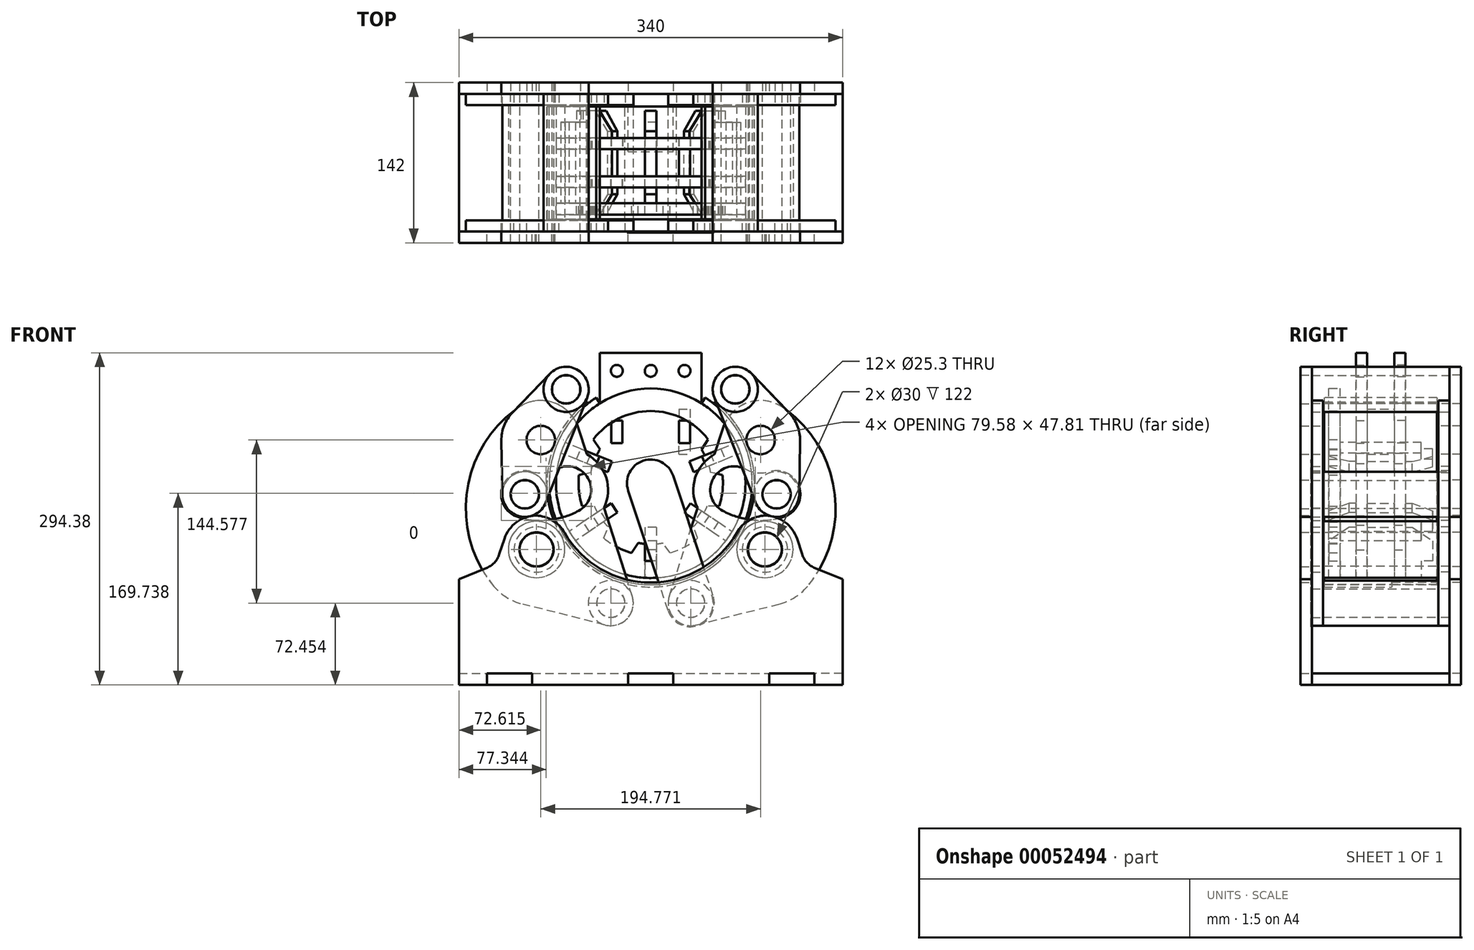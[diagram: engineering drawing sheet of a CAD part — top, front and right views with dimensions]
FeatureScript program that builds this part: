
annotation { "Feature Type Name" : "Feature", "Feature Type Description" : "" }
export const myFeature = defineFeature(function(context is Context, id is Id, definition is map)
    precondition{}
    {
        {
            var Q0;
            Q0=qCreatedBy(makeId("Front.planeOp"),FACE);
            var sketch = newSketch(context, id + "F0", { "sketchPlane" : qUnion([Q0])});
            skCircle(sketch, "E0", {"center": v(0, 0) * mm, "radius": 90 * mm, "construction": true});
            skLineSegment(sketch, "E1", {"start": v(0, -90) * mm, "end": v(0, 90) * mm, "construction": true});
            skLineSegment(sketch, "E2", {"start": v(0, 0) * mm, "end": v(-55.75, 70.66) * mm, "construction": true});
            skLineSegment(sketch, "E3", {"start": v(0, 0) * mm, "end": v(55.75, 70.66) * mm, "construction": true});
            skArc(sketch, "E4", {"start": v(-55.75, 70.66) * mm, "mid": v(0, -90) * mm, "end": v(55.75, 70.66) * mm});
            skArc(sketch, "E5", {"start": v(-56.98, 72.23) * mm, "mid": v(0, -92) * mm, "end": v(56.98, 72.23) * mm});
            skLineSegment(sketch, "E6", {"start": v(-56.98, 72.23) * mm, "end": v(-55.75, 70.66) * mm});
            skLineSegment(sketch, "E7", {"start": v(55.75, 70.66) * mm, "end": v(56.98, 72.23) * mm});
            skSolve(sketch);
        }
        {
            var Q0;
            Q0 = qSketchRegion(id + "F0", true);
            extrude(context, id + "F1", {"entities" : qUnion([Q0]), "depth" : 100 * mm});
        }
        {
            var Q0;
            Q0=qCreatedBy(makeId("Top.planeOp"),FACE);
            var sketch = newSketch(context, id + "F2", { "sketchPlane" : qUnion([Q0])});
            skLineSegment(sketch, "E8.bottom", {"start": v(-20, 0) * mm, "end": v(20, 0) * mm});
            skLineSegment(sketch, "E8.top", {"start": v(-20, -40) * mm, "end": v(20, -40) * mm});
            skLineSegment(sketch, "E8.left", {"start": v(-20, 0) * mm, "end": v(-20, -40) * mm});
            skLineSegment(sketch, "E8.right", {"start": v(20, 0) * mm, "end": v(20, -40) * mm});
            skLineSegment(sketch, "E9", {"start": v(0, 0) * mm, "end": v(0, -89.55) * mm, "construction": true});
            skSolve(sketch);
        }
        {
            var Q0;
            Q0 = qSketchRegion(id + "F2", true);
            extrude(context, id + "F3", {"entities" : qUnion([Q0]), "operationType" : NewBodyOperationType.REMOVE, "endBound" : BoundingType.THROUGH_ALL, "oppositeDirection" : true, "depth" : 25 * mm});
        }
        {
            var Q0;
            Q0=qCreatedBy(makeId("Front.planeOp"),FACE);
            var sketch = newSketch(context, id + "F4", { "sketchPlane" : qUnion([Q0])});
            skCircle(sketch, "E10", {"center": v(74.96, 83.22) * mm, "radius": 20 * mm});
            skCircle(sketch, "E11", {"center": v(74.96, 83.22) * mm, "radius": 12.5 * mm});
            skLineSegment(sketch, "E12", {"start": v(0, 0) * mm, "end": v(74.96, 83.22) * mm, "construction": true});
            skSolve(sketch);
        }
        {
            var Q0;
            Q0 = qSketchRegion(id + "F4", true);
            extrude(context, id + "F5", {"entities" : qUnion([Q0]), "depth" : 111 * mm, "hasSecondDirection" : true, "secondDirectionOppositeDirection" : true, "secondDirectionDepth" : 11 * mm});
        }
        {
            var Q0;
            Q0=qCreatedBy(makeId("Front.planeOp"),FACE);
            var sketch = newSketch(context, id + "F6", { "sketchPlane" : qUnion([Q0])});
            skCircle(sketch, "E13", {"center": v(35.38, -106.27) * mm, "radius": 20 * mm});
            skCircle(sketch, "E14", {"center": v(35.38, -106.27) * mm, "radius": 12.5 * mm});
            skLineSegment(sketch, "E15", {"start": v(0, 0) * mm, "end": v(0, -124.08) * mm, "construction": true});
            skLineSegment(sketch, "E16", {"start": v(35.38, -106.27) * mm, "end": v(74.96, 83.22) * mm, "construction": true});
            skLineSegment(sketch, "E17", {"start": v(47.65, -47.53) * mm, "end": v(101.2, -58.72) * mm, "construction": true});
            skCircle(sketch, "E18", {"center": v(101.2, -58.72) * mm, "radius": 101.2 * mm, "construction": true});
            skLineSegment(sketch, "E19", {"start": v(0, 0) * mm, "end": v(35.38, -106.27) * mm, "construction": true});
            skPoint(sketch, "E20", {"position": v(29.06, -87.3) * mm});
            skCircle(sketch, "E21", {"center": v(101.2, -58.72) * mm, "radius": 25 * mm, "construction": true});
            skSolve(sketch);
        }
        {
            var Q0;
            Q0 = qSketchRegion(id + "F6", true);
            extrude(context, id + "F7", {"entities" : qUnion([Q0]), "depth" : 101 * mm, "hasSecondDirection" : true, "secondDirectionOppositeDirection" : true, "secondDirectionDepth" : 1 * mm});
        }
        {
            var Q0;
            Q0=qCreatedBy(makeId("Front.planeOp"),FACE);
            var sketch = newSketch(context, id + "F8", { "sketchPlane" : qUnion([Q0])});
            skCircle(sketch, "E22", {"center": v(111.57, -9.84) * mm, "radius": 20 * mm});
            skCircle(sketch, "E23", {"center": v(111.57, -9.84) * mm, "radius": 12.5 * mm});
            skSolve(sketch);
        }
        {
            var Q0;
            Q0 = qSketchRegion(id + "F8", true);
            extrude(context, id + "F9", {"entities" : qUnion([Q0]), "depth" : 111 * mm, "hasSecondDirection" : true, "secondDirectionOppositeDirection" : true, "secondDirectionDepth" : 11 * mm});
        }
        {
            var Q0;
            Q0=makeQuery(id+"F5.opExtrude","CAP_FACE",FACE,{"disambiguationData":[OSD([sQuery(id+"F4.wireOp",EDGE,"E10"),sQuery(id+"F4.wireOp",EDGE,"E11")])],"isStart":false});
            var sketch = newSketch(context, id + "F10", { "sketchPlane" : qUnion([Q0])});
            skCircle(sketch, "E24", {"center": v(74.96, 83.22) * mm, "radius": 12.6 * mm});
            skCircle(sketch, "E25", {"center": v(111.57, -9.84) * mm, "radius": 12.6 * mm});
            skLineSegment(sketch, "E26", {"start": v(74.96, 83.22) * mm, "end": v(111.57, -9.84) * mm, "construction": true});
            skLineSegment(sketch, "E27", {"start": v(89.36, 97.1) * mm, "end": v(122.6, 62.6) * mm});
            skLineSegment(sketch, "E28", {"start": v(131.56, -10.18) * mm, "end": v(132.38, 37.71) * mm});
            skArc(sketch, "E29", {"start": v(132.38, 37.71) * mm, "mid": v(129.96, 51.12) * mm, "end": v(122.6, 62.6) * mm});
            skArc(sketch, "E30", {"start": v(89.36, 97.1) * mm, "mid": v(64.15, 100.05) * mm, "end": v(56.35, 75.9) * mm});
            skArc(sketch, "E31", {"start": v(92.96, -17.16) * mm, "mid": v(115.13, -29.52) * mm, "end": v(131.56, -10.18) * mm});
            skLineSegment(sketch, "E32", {"start": v(56.35, 75.9) * mm, "end": v(92.96, -17.16) * mm});
            skCircle(sketch, "E33", {"center": v(97.39, 38.31) * mm, "radius": 12.65 * mm});
            skLineSegment(sketch, "E34", {"start": v(97.39, 38.31) * mm, "end": v(93.26, 36.69) * mm, "construction": true});
            skSolve(sketch);
        }
        {
            var Q0;
            Q0 = qSketchRegion(id + "F10", true);
            extrude(context, id + "F11", {"entities" : qUnion([Q0]), "depth" : 10 * mm});
        }
        {
            var Q0;
            Q0=makeQuery(id+"F7.opExtrude","CAP_FACE",FACE,{"disambiguationData":[OSD([sQuery(id+"F6.wireOp",EDGE,"E13"),sQuery(id+"F6.wireOp",EDGE,"E14")])],"isStart":false});
            var sketch = newSketch(context, id + "F12", { "sketchPlane" : qUnion([Q0])});
            skCircle(sketch, "E35", {"center": v(97.39, 38.31) * mm, "radius": 12.65 * mm});
            skCircle(sketch, "E36", {"center": v(101.2, -58.72) * mm, "radius": 20 * mm});
            skCircle(sketch, "E37", {"center": v(35.38, -106.27) * mm, "radius": 12.65 * mm});
            skArc(sketch, "E38", {"start": v(16.33, -100.17) * mm, "mid": v(20.8, -119.96) * mm, "end": v(40.27, -125.66) * mm});
            skArc(sketch, "E39", {"start": v(117.45, 67) * mm, "mid": v(86.2, 71.47) * mm, "end": v(64.05, 48.98) * mm});
            skArc(sketch, "E40", {"start": v(113.43, -107.2) * mm, "mid": v(128.35, -100.7) * mm, "end": v(140.4, -89.75) * mm});
            skArc(sketch, "E41", {"start": v(140.4, -89.75) * mm, "mid": v(162.75, -6.43) * mm, "end": v(117.45, 67) * mm});
            skLineSegment(sketch, "E42", {"start": v(16.33, -100.17) * mm, "end": v(41.41, -21.77) * mm});
            skLineSegment(sketch, "E43", {"start": v(40.27, -125.66) * mm, "end": v(113.43, -107.2) * mm});
            skPoint(sketch, "E44.visualSharp", {"position": v(128.63, -50.95) * mm});
            skCircle(sketch, "E45", {"center": v(97.39, 38.31) * mm, "radius": 50.2 * mm, "construction": true});
            skPoint(sketch, "E46", {"position": v(111.57, -9.84) * mm});
            skArc(sketch, "E47", {"start": v(73.76, -5.98) * mm, "mid": v(92.29, -11.63) * mm, "end": v(111.57, -9.84) * mm});
            skArc(sketch, "E48.0.startCap", {"start": v(63.88, -24.5) * mm, "mid": v(55.23, 3.9) * mm, "end": v(83.65, 12.55) * mm});
            skArc(sketch, "E48.0.endCap", {"start": v(105.63, 10.3) * mm, "mid": v(131.71, -3.9) * mm, "end": v(117.5, -29.98) * mm});
            skArc(sketch, "E48.0.left", {"start": v(83.65, 12.55) * mm, "mid": v(94.42, 9.27) * mm, "end": v(105.63, 10.3) * mm});
            skArc(sketch, "E48.0.right", {"start": v(63.88, -24.5) * mm, "mid": v(90.15, -32.52) * mm, "end": v(117.5, -29.98) * mm});
            skArc(sketch, "E49", {"start": v(56.59, 25.66) * mm, "mid": v(39.48, 5) * mm, "end": v(41.41, -21.77) * mm});
            skLineSegment(sketch, "E50.trimOffspring", {"start": v(56.59, 25.66) * mm, "end": v(64.05, 48.98) * mm});
            skSolve(sketch);
        }
        {
            var Q0;
            Q0 = qSketchRegion(id + "F12", true);
            extrude(context, id + "F13", {"entities" : qUnion([Q0]), "depth" : 10 * mm});
        }
        {
            var Q0;
            Q0=makeQuery(id+"F9.opExtrude","CAP_FACE",FACE,{"disambiguationData":[OSD([sQuery(id+"F8.wireOp",EDGE,"E22"),sQuery(id+"F8.wireOp",EDGE,"E23")])],"isStart":false});
            var Q1;
            Q1=makeQuery(id+"F9.opExtrude","CAP_FACE",FACE,{"disambiguationData":[OSD([sQuery(id+"F8.wireOp",EDGE,"E22"),sQuery(id+"F8.wireOp",EDGE,"E23")])],"isStart":true});
            cPlane(context, id + "F14", {"entities" : qUnion([Q0, Q1]), "cplaneType" : CPlaneType.MID_PLANE, "offset" : 150 * mm, "width" : 150 * mm, "height" : 150 * mm});
        }
        {
            var Q0;
            Q0=makeQuery(id+"F13.opExtrude","SWEPT_BODY",BODY,{"disambiguationData":[OSD([sQuery(id+"F12.wireOp",EDGE,"E35"),sQuery(id+"F12.wireOp",EDGE,"E36"),sQuery(id+"F12.wireOp",EDGE,"E37"),sQuery(id+"F12.wireOp",EDGE,"E38"),sQuery(id+"F12.wireOp",EDGE,"E39"),sQuery(id+"F12.wireOp",EDGE,"E40"),sQuery(id+"F12.wireOp",EDGE,"E41"),sQuery(id+"F12.wireOp",EDGE,"E42"),sQuery(id+"F12.wireOp",EDGE,"E43"),sQuery(id+"F12.wireOp",EDGE,"E48.0.startCap"),sQuery(id+"F12.wireOp",EDGE,"E48.0.endCap"),sQuery(id+"F12.wireOp",EDGE,"E48.0.left"),sQuery(id+"F12.wireOp",EDGE,"E48.0.right"),sQuery(id+"F12.wireOp",EDGE,"E49"),sQuery(id+"F12.wireOp",EDGE,"E50.trimOffspring")])]});
            var Q1;
            Q1=makeQuery(id+"F11.opExtrude","SWEPT_BODY",BODY,{"disambiguationData":[OSD([sQuery(id+"F10.wireOp",EDGE,"E24"),sQuery(id+"F10.wireOp",EDGE,"E25"),sQuery(id+"F10.wireOp",EDGE,"E27"),sQuery(id+"F10.wireOp",EDGE,"E28"),sQuery(id+"F10.wireOp",EDGE,"E29"),sQuery(id+"F10.wireOp",EDGE,"E30"),sQuery(id+"F10.wireOp",EDGE,"E31"),sQuery(id+"F10.wireOp",EDGE,"E32"),sQuery(id+"F10.wireOp",EDGE,"E33")])]});
            var Q2;
            Q2=qCreatedBy(id+"F14.planeOp",FACE);
            mirror(context, id + "F15", {"entities" : qUnion([Q0, Q1]), "mirrorPlane" : qUnion([Q2])});
        }
        {
            var Q0;
            Q0=makeQuery(id+"F13.opExtrude","CAP_FACE",FACE,{"disambiguationData":[OSD([sQuery(id+"F12.wireOp",EDGE,"E35"),sQuery(id+"F12.wireOp",EDGE,"E36"),sQuery(id+"F12.wireOp",EDGE,"E37"),sQuery(id+"F12.wireOp",EDGE,"E38"),sQuery(id+"F12.wireOp",EDGE,"E39"),sQuery(id+"F12.wireOp",EDGE,"E40"),sQuery(id+"F12.wireOp",EDGE,"E41"),sQuery(id+"F12.wireOp",EDGE,"E42"),sQuery(id+"F12.wireOp",EDGE,"E43"),sQuery(id+"F12.wireOp",EDGE,"E48.0.startCap"),sQuery(id+"F12.wireOp",EDGE,"E48.0.endCap"),sQuery(id+"F12.wireOp",EDGE,"E48.0.left"),sQuery(id+"F12.wireOp",EDGE,"E48.0.right"),sQuery(id+"F12.wireOp",EDGE,"E49"),sQuery(id+"F12.wireOp",EDGE,"E50.trimOffspring")])],"isStart":false});
            var sketch = newSketch(context, id + "F16", { "sketchPlane" : qUnion([Q0])});
            skCircle(sketch, "E51", {"center": v(101.2, -58.72) * mm, "radius": 25 * mm});
            skCircle(sketch, "E52", {"center": v(101.2, -58.72) * mm, "radius": 15 * mm});
            skSolve(sketch);
        }
        {
            var Q0;
            Q0 = qSketchRegion(id + "F16", true);
            var Q1;
            Q1=makeQuery(id+"F15.opPattern","COPY",FACE,{"derivedFrom":makeQuery(id+"F13.opExtrude","CAP_FACE",FACE,{"disambiguationData":[OSD([sQuery(id+"F12.wireOp",EDGE,"E35"),sQuery(id+"F12.wireOp",EDGE,"E36"),sQuery(id+"F12.wireOp",EDGE,"E37"),sQuery(id+"F12.wireOp",EDGE,"E38"),sQuery(id+"F12.wireOp",EDGE,"E39"),sQuery(id+"F12.wireOp",EDGE,"E40"),sQuery(id+"F12.wireOp",EDGE,"E41"),sQuery(id+"F12.wireOp",EDGE,"E42"),sQuery(id+"F12.wireOp",EDGE,"E43"),sQuery(id+"F12.wireOp",EDGE,"E48.0.startCap"),sQuery(id+"F12.wireOp",EDGE,"E48.0.endCap"),sQuery(id+"F12.wireOp",EDGE,"E48.0.left"),sQuery(id+"F12.wireOp",EDGE,"E48.0.right"),sQuery(id+"F12.wireOp",EDGE,"E49"),sQuery(id+"F12.wireOp",EDGE,"E50.trimOffspring")])],"isStart":false}),"instanceName":"1"});
            extrude(context, id + "F17", {"entities" : qUnion([Q0]), "endBound" : BoundingType.UP_TO_SURFACE, "oppositeDirection" : true, "endBoundEntityFace" : qUnion([Q1]), "depth" : 25 * mm});
        }
        {
            var Q0;
            Q0=makeQuery(id+"F13.opExtrude","SWEPT_BODY",BODY,{"disambiguationData":[OSD([sQuery(id+"F12.wireOp",EDGE,"E35"),sQuery(id+"F12.wireOp",EDGE,"E36"),sQuery(id+"F12.wireOp",EDGE,"E37"),sQuery(id+"F12.wireOp",EDGE,"E38"),sQuery(id+"F12.wireOp",EDGE,"E39"),sQuery(id+"F12.wireOp",EDGE,"E40"),sQuery(id+"F12.wireOp",EDGE,"E41"),sQuery(id+"F12.wireOp",EDGE,"E42"),sQuery(id+"F12.wireOp",EDGE,"E43"),sQuery(id+"F12.wireOp",EDGE,"E48.0.startCap"),sQuery(id+"F12.wireOp",EDGE,"E48.0.endCap"),sQuery(id+"F12.wireOp",EDGE,"E48.0.left"),sQuery(id+"F12.wireOp",EDGE,"E48.0.right"),sQuery(id+"F12.wireOp",EDGE,"E49"),sQuery(id+"F12.wireOp",EDGE,"E50.trimOffspring")])]});
            var Q1;
            Q1=makeQuery(id+"F15.opPattern","COPY",BODY,{"derivedFrom":makeQuery(id+"F13.opExtrude","SWEPT_BODY",BODY,{"disambiguationData":[OSD([sQuery(id+"F12.wireOp",EDGE,"E35"),sQuery(id+"F12.wireOp",EDGE,"E36"),sQuery(id+"F12.wireOp",EDGE,"E37"),sQuery(id+"F12.wireOp",EDGE,"E38"),sQuery(id+"F12.wireOp",EDGE,"E39"),sQuery(id+"F12.wireOp",EDGE,"E40"),sQuery(id+"F12.wireOp",EDGE,"E41"),sQuery(id+"F12.wireOp",EDGE,"E42"),sQuery(id+"F12.wireOp",EDGE,"E43"),sQuery(id+"F12.wireOp",EDGE,"E48.0.startCap"),sQuery(id+"F12.wireOp",EDGE,"E48.0.endCap"),sQuery(id+"F12.wireOp",EDGE,"E48.0.left"),sQuery(id+"F12.wireOp",EDGE,"E48.0.right"),sQuery(id+"F12.wireOp",EDGE,"E49"),sQuery(id+"F12.wireOp",EDGE,"E50.trimOffspring")])]}),"instanceName":"1"});
            var Q2;
            Q2=makeQuery(id+"F17.opExtrude","SWEPT_BODY",BODY,{"disambiguationData":[OSD([sQuery(id+"F16.wireOp",EDGE,"E51"),sQuery(id+"F16.wireOp",EDGE,"E52")])]});
            booleanBodies(context, id + "F18", {"operationType" : BooleanOperationType.SUBTRACTION, "tools" : qUnion([Q0, Q1]), "targets" : qUnion([Q2]), "keepTools" : true});
        }
        {
            var Q0;
            Q0=makeQuery(id+"F11.opExtrude","SWEPT_BODY",BODY,{"disambiguationData":[OSD([sQuery(id+"F10.wireOp",EDGE,"E24"),sQuery(id+"F10.wireOp",EDGE,"E25"),sQuery(id+"F10.wireOp",EDGE,"E27"),sQuery(id+"F10.wireOp",EDGE,"E28"),sQuery(id+"F10.wireOp",EDGE,"E29"),sQuery(id+"F10.wireOp",EDGE,"E30"),sQuery(id+"F10.wireOp",EDGE,"E31"),sQuery(id+"F10.wireOp",EDGE,"E32"),sQuery(id+"F10.wireOp",EDGE,"E33")])]});
            var Q1;
            Q1=makeQuery(id+"F13.opExtrude","SWEPT_BODY",BODY,{"disambiguationData":[OSD([sQuery(id+"F12.wireOp",EDGE,"E35"),sQuery(id+"F12.wireOp",EDGE,"E36"),sQuery(id+"F12.wireOp",EDGE,"E37"),sQuery(id+"F12.wireOp",EDGE,"E38"),sQuery(id+"F12.wireOp",EDGE,"E39"),sQuery(id+"F12.wireOp",EDGE,"E40"),sQuery(id+"F12.wireOp",EDGE,"E41"),sQuery(id+"F12.wireOp",EDGE,"E42"),sQuery(id+"F12.wireOp",EDGE,"E43"),sQuery(id+"F12.wireOp",EDGE,"E48.0.startCap"),sQuery(id+"F12.wireOp",EDGE,"E48.0.endCap"),sQuery(id+"F12.wireOp",EDGE,"E48.0.left"),sQuery(id+"F12.wireOp",EDGE,"E48.0.right"),sQuery(id+"F12.wireOp",EDGE,"E49"),sQuery(id+"F12.wireOp",EDGE,"E50.trimOffspring")])]});
            var Q2;
            Q2=makeQuery(id+"F7.opExtrude","SWEPT_BODY",BODY,{"disambiguationData":[OSD([sQuery(id+"F6.wireOp",EDGE,"E13"),sQuery(id+"F6.wireOp",EDGE,"E14")])]});
            var Q3;
            Q3=makeQuery(id+"F17.opExtrude","SWEPT_BODY",BODY,{"disambiguationData":[OSD([sQuery(id+"F16.wireOp",EDGE,"E51"),sQuery(id+"F16.wireOp",EDGE,"E52")])]});
            var Q4;
            Q4=makeQuery(id+"F15.opPattern","COPY",BODY,{"derivedFrom":makeQuery(id+"F13.opExtrude","SWEPT_BODY",BODY,{"disambiguationData":[OSD([sQuery(id+"F12.wireOp",EDGE,"E35"),sQuery(id+"F12.wireOp",EDGE,"E36"),sQuery(id+"F12.wireOp",EDGE,"E37"),sQuery(id+"F12.wireOp",EDGE,"E38"),sQuery(id+"F12.wireOp",EDGE,"E39"),sQuery(id+"F12.wireOp",EDGE,"E40"),sQuery(id+"F12.wireOp",EDGE,"E41"),sQuery(id+"F12.wireOp",EDGE,"E42"),sQuery(id+"F12.wireOp",EDGE,"E43"),sQuery(id+"F12.wireOp",EDGE,"E48.0.startCap"),sQuery(id+"F12.wireOp",EDGE,"E48.0.endCap"),sQuery(id+"F12.wireOp",EDGE,"E48.0.left"),sQuery(id+"F12.wireOp",EDGE,"E48.0.right"),sQuery(id+"F12.wireOp",EDGE,"E49"),sQuery(id+"F12.wireOp",EDGE,"E50.trimOffspring")])]}),"instanceName":"1"});
            var Q5;
            Q5=makeQuery(id+"F15.opPattern","COPY",BODY,{"derivedFrom":makeQuery(id+"F11.opExtrude","SWEPT_BODY",BODY,{"disambiguationData":[OSD([sQuery(id+"F10.wireOp",EDGE,"E24"),sQuery(id+"F10.wireOp",EDGE,"E25"),sQuery(id+"F10.wireOp",EDGE,"E27"),sQuery(id+"F10.wireOp",EDGE,"E28"),sQuery(id+"F10.wireOp",EDGE,"E29"),sQuery(id+"F10.wireOp",EDGE,"E30"),sQuery(id+"F10.wireOp",EDGE,"E31"),sQuery(id+"F10.wireOp",EDGE,"E32"),sQuery(id+"F10.wireOp",EDGE,"E33")])]}),"instanceName":"1"});
            var Q6;
            Q6=makeQuery(id+"F5.opExtrude","SWEPT_BODY",BODY,{"disambiguationData":[OSD([sQuery(id+"F4.wireOp",EDGE,"E10"),sQuery(id+"F4.wireOp",EDGE,"E11")])]});
            var Q7;
            Q7=makeQuery(id+"F9.opExtrude","SWEPT_BODY",BODY,{"disambiguationData":[OSD([sQuery(id+"F8.wireOp",EDGE,"E22"),sQuery(id+"F8.wireOp",EDGE,"E23")])]});
            var Q8;
            Q8=qCreatedBy(makeId("Right.planeOp"),FACE);
            mirror(context, id + "F19", {"entities" : qUnion([Q0, Q1, Q2, Q3, Q4, Q5, Q6, Q7]), "mirrorPlane" : qUnion([Q8])});
        }
        {
            var Q0;
            Q0=makeQuery(id+"F13.opExtrude","CAP_FACE",FACE,{"disambiguationData":[OSD([sQuery(id+"F12.wireOp",EDGE,"E35"),sQuery(id+"F12.wireOp",EDGE,"E36"),sQuery(id+"F12.wireOp",EDGE,"E37"),sQuery(id+"F12.wireOp",EDGE,"E38"),sQuery(id+"F12.wireOp",EDGE,"E39"),sQuery(id+"F12.wireOp",EDGE,"E40"),sQuery(id+"F12.wireOp",EDGE,"E41"),sQuery(id+"F12.wireOp",EDGE,"E42"),sQuery(id+"F12.wireOp",EDGE,"E43"),sQuery(id+"F12.wireOp",EDGE,"E48.0.startCap"),sQuery(id+"F12.wireOp",EDGE,"E48.0.endCap"),sQuery(id+"F12.wireOp",EDGE,"E48.0.left"),sQuery(id+"F12.wireOp",EDGE,"E48.0.right"),sQuery(id+"F12.wireOp",EDGE,"E49"),sQuery(id+"F12.wireOp",EDGE,"E50.trimOffspring")])],"isStart":false});
            var sketch = newSketch(context, id + "F20", { "sketchPlane" : qUnion([Q0])});
            skCircle(sketch, "E53", {"center": v(101.2, -58.72) * mm, "radius": 15.15 * mm});
            skCircle(sketch, "E54", {"center": v(-101.2, -58.72) * mm, "radius": 15.15 * mm});
            skLineSegment(sketch, "E55.bottom", {"start": v(-102.35, -28.72) * mm, "end": v(-101.2, -28.72) * mm});
            skLineSegment(sketch, "E55.top", {"start": v(-145, -178.72) * mm, "end": v(-145, -178.72) * mm});
            skLineSegment(sketch, "E56.top", {"start": v(-145, -168.72) * mm, "end": v(-105, -168.72) * mm});
            skLineSegment(sketch, "E56.left", {"start": v(-145, -178.72) * mm, "end": v(-145, -168.72) * mm});
            skLineSegment(sketch, "E56.right", {"start": v(-105, -178.72) * mm, "end": v(-105, -168.72) * mm});
            skLineSegment(sketch, "E57.top", {"start": v(105, -168.72) * mm, "end": v(145, -168.72) * mm});
            skLineSegment(sketch, "E57.left", {"start": v(105, -178.72) * mm, "end": v(105, -168.72) * mm});
            skLineSegment(sketch, "E57.right", {"start": v(145, -178.72) * mm, "end": v(145, -168.72) * mm});
            skLineSegment(sketch, "E58.top", {"start": v(-20, -168.72) * mm, "end": v(20, -168.72) * mm});
            skLineSegment(sketch, "E58.left", {"start": v(-20, -178.72) * mm, "end": v(-20, -168.72) * mm});
            skLineSegment(sketch, "E58.right", {"start": v(20, -178.72) * mm, "end": v(20, -168.72) * mm});
            skLineSegment(sketch, "E59", {"start": v(0, -178.72) * mm, "end": v(0, -28.72) * mm, "construction": true});
            skLineSegment(sketch, "E60.trimOffspring", {"start": v(-105, -178.72) * mm, "end": v(-20, -178.72) * mm});
            skLineSegment(sketch, "E61.trimOffspring", {"start": v(20, -178.72) * mm, "end": v(105, -178.72) * mm});
            skLineSegment(sketch, "E62.trimOffspring", {"start": v(145, -178.72) * mm, "end": v(170, -178.72) * mm});
            skPoint(sketch, "E63.visualSharp", {"position": v(-131.2, -28.72) * mm});
            skArc(sketch, "E63.filletArc", {"start": v(-101.2, -28.72) * mm, "mid": v(-118.77, -34.4) * mm, "end": v(-129.68, -49.3) * mm});
            skPoint(sketch, "E64.visualSharp", {"position": v(131.2, -28.72) * mm});
            skArc(sketch, "E65", {"start": v(-76.33, -43.8) * mm, "mid": v(0, -88) * mm, "end": v(76.33, -43.8) * mm});
            skLineSegment(sketch, "E66.trimOffspring", {"start": v(101.2, -28.72) * mm, "end": v(102.35, -28.72) * mm});
            skPoint(sketch, "E67.visualSharp", {"position": v(-83.18, -28.72) * mm});
            skArc(sketch, "E67.filletArc", {"start": v(-76.33, -43.8) * mm, "mid": v(-87.32, -32.76) * mm, "end": v(-102.35, -28.72) * mm});
            skPoint(sketch, "E68.visualSharp", {"position": v(83.18, -28.72) * mm});
            skArc(sketch, "E68.filletArc", {"start": v(102.35, -28.72) * mm, "mid": v(87.32, -32.76) * mm, "end": v(76.33, -43.8) * mm});
            skArc(sketch, "E69", {"start": v(-145.7, -75.26) * mm, "mid": v(-138.6, -70.4) * mm, "end": v(-134.2, -63) * mm});
            skLineSegment(sketch, "E70", {"start": v(-129.68, -49.3) * mm, "end": v(-134.2, -63) * mm});
            skLineSegment(sketch, "E71", {"start": v(-145.7, -75.26) * mm, "end": v(-170, -85.08) * mm});
            skLineSegment(sketch, "E72", {"start": v(-170, -85.08) * mm, "end": v(-170, -178.72) * mm});
            skLineSegment(sketch, "E73", {"start": v(-170, -178.72) * mm, "end": v(-145, -178.72) * mm});
            skLineSegment(sketch, "E74.MirrorCS", {"start": v(170, -85.08) * mm, "end": v(170, -178.72) * mm});
            skLineSegment(sketch, "E75.MirrorCS", {"start": v(145.7, -75.26) * mm, "end": v(170, -85.08) * mm});
            skArc(sketch, "E76.MirrorC", {"start": v(145.7, -75.26) * mm, "mid": v(138.6, -70.4) * mm, "end": v(134.2, -63) * mm});
            skLineSegment(sketch, "E77.MirrorCS", {"start": v(129.68, -49.3) * mm, "end": v(134.2, -63) * mm});
            skArc(sketch, "E78.MirrorCS", {"start": v(101.2, -28.72) * mm, "mid": v(118.77, -34.4) * mm, "end": v(129.68, -49.3) * mm});
            skSolve(sketch);
        }
        {
            var Q0;
            Q0 = qSketchRegion(id + "F20", true);
            extrude(context, id + "F21", {"entities" : qUnion([Q0]), "depth" : 10 * mm});
        }
        {
            var Q0;
            Q0=makeQuery(id+"F21.opExtrude","SWEPT_BODY",BODY,{"disambiguationData":[OSD([sQuery(id+"F20.wireOp",EDGE,"E53"),sQuery(id+"F20.wireOp",EDGE,"E54"),sQuery(id+"F20.wireOp",EDGE,"E55.bottom"),sQuery(id+"F20.wireOp",EDGE,"E56.top"),sQuery(id+"F20.wireOp",EDGE,"E56.left"),sQuery(id+"F20.wireOp",EDGE,"E56.right"),sQuery(id+"F20.wireOp",EDGE,"E57.top"),sQuery(id+"F20.wireOp",EDGE,"E57.left"),sQuery(id+"F20.wireOp",EDGE,"E57.right"),sQuery(id+"F20.wireOp",EDGE,"E58.top"),sQuery(id+"F20.wireOp",EDGE,"E58.left"),sQuery(id+"F20.wireOp",EDGE,"E58.right"),sQuery(id+"F20.wireOp",EDGE,"E60.trimOffspring"),sQuery(id+"F20.wireOp",EDGE,"E61.trimOffspring"),sQuery(id+"F20.wireOp",EDGE,"E62.trimOffspring"),sQuery(id+"F20.wireOp",EDGE,"E63.filletArc"),sQuery(id+"F20.wireOp",EDGE,"E65"),sQuery(id+"F20.wireOp",EDGE,"E66.trimOffspring"),sQuery(id+"F20.wireOp",EDGE,"E67.filletArc"),sQuery(id+"F20.wireOp",EDGE,"E68.filletArc"),sQuery(id+"F20.wireOp",EDGE,"E69"),sQuery(id+"F20.wireOp",EDGE,"E70"),sQuery(id+"F20.wireOp",EDGE,"E71"),sQuery(id+"F20.wireOp",EDGE,"E72"),sQuery(id+"F20.wireOp",EDGE,"E73"),sQuery(id+"F20.wireOp",EDGE,"E74.MirrorCS"),sQuery(id+"F20.wireOp",EDGE,"E75.MirrorCS"),sQuery(id+"F20.wireOp",EDGE,"E76.MirrorC"),sQuery(id+"F20.wireOp",EDGE,"E77.MirrorCS"),sQuery(id+"F20.wireOp",EDGE,"E78.MirrorCS")])]});
            var Q1;
            Q1=qCreatedBy(id+"F14.planeOp",FACE);
            mirror(context, id + "F22", {"entities" : qUnion([Q0]), "mirrorPlane" : qUnion([Q1])});
        }
        {
            var Q0;
            Q0=makeQuery(id+"F21.opExtrude","SWEPT_FACE",FACE,{"disambiguationData":[OSD([sQuery(id+"F20.wireOp",EDGE,"E73")])]});
            var sketch = newSketch(context, id + "F23", { "sketchPlane" : qUnion([Q0])});
            skLineSegment(sketch, "E79.bottom", {"start": v(-170, 121) * mm, "end": v(170, 121) * mm});
            skLineSegment(sketch, "E79.top", {"start": v(-170, -21) * mm, "end": v(170, -21) * mm});
            skLineSegment(sketch, "E79.left", {"start": v(-170, 121) * mm, "end": v(-170, -21) * mm});
            skLineSegment(sketch, "E79.right", {"start": v(170, 121) * mm, "end": v(170, -21) * mm});
            skSolve(sketch);
        }
        {
            var Q0;
            Q0 = qSketchRegion(id + "F23", true);
            extrude(context, id + "F24", {"entities" : qUnion([Q0]), "oppositeDirection" : true, "depth" : 10 * mm});
        }
        {
            var Q0;
            Q0=makeQuery(id+"F21.opExtrude","SWEPT_BODY",BODY,{"disambiguationData":[OSD([sQuery(id+"F20.wireOp",EDGE,"E53"),sQuery(id+"F20.wireOp",EDGE,"E54"),sQuery(id+"F20.wireOp",EDGE,"E55.bottom"),sQuery(id+"F20.wireOp",EDGE,"E56.top"),sQuery(id+"F20.wireOp",EDGE,"E56.left"),sQuery(id+"F20.wireOp",EDGE,"E56.right"),sQuery(id+"F20.wireOp",EDGE,"E57.top"),sQuery(id+"F20.wireOp",EDGE,"E57.left"),sQuery(id+"F20.wireOp",EDGE,"E57.right"),sQuery(id+"F20.wireOp",EDGE,"E58.top"),sQuery(id+"F20.wireOp",EDGE,"E58.left"),sQuery(id+"F20.wireOp",EDGE,"E58.right"),sQuery(id+"F20.wireOp",EDGE,"E60.trimOffspring"),sQuery(id+"F20.wireOp",EDGE,"E61.trimOffspring"),sQuery(id+"F20.wireOp",EDGE,"E62.trimOffspring"),sQuery(id+"F20.wireOp",EDGE,"E63.filletArc"),sQuery(id+"F20.wireOp",EDGE,"E65"),sQuery(id+"F20.wireOp",EDGE,"E66.trimOffspring"),sQuery(id+"F20.wireOp",EDGE,"E67.filletArc"),sQuery(id+"F20.wireOp",EDGE,"E68.filletArc"),sQuery(id+"F20.wireOp",EDGE,"E69"),sQuery(id+"F20.wireOp",EDGE,"E70"),sQuery(id+"F20.wireOp",EDGE,"E71"),sQuery(id+"F20.wireOp",EDGE,"E72"),sQuery(id+"F20.wireOp",EDGE,"E73"),sQuery(id+"F20.wireOp",EDGE,"E74.MirrorCS"),sQuery(id+"F20.wireOp",EDGE,"E75.MirrorCS"),sQuery(id+"F20.wireOp",EDGE,"E76.MirrorC"),sQuery(id+"F20.wireOp",EDGE,"E77.MirrorCS"),sQuery(id+"F20.wireOp",EDGE,"E78.MirrorCS")])]});
            var Q1;
            Q1=makeQuery(id+"F22.opPattern","COPY",BODY,{"derivedFrom":makeQuery(id+"F21.opExtrude","SWEPT_BODY",BODY,{"disambiguationData":[OSD([sQuery(id+"F20.wireOp",EDGE,"E53"),sQuery(id+"F20.wireOp",EDGE,"E54"),sQuery(id+"F20.wireOp",EDGE,"E55.bottom"),sQuery(id+"F20.wireOp",EDGE,"E56.top"),sQuery(id+"F20.wireOp",EDGE,"E56.left"),sQuery(id+"F20.wireOp",EDGE,"E56.right"),sQuery(id+"F20.wireOp",EDGE,"E57.top"),sQuery(id+"F20.wireOp",EDGE,"E57.left"),sQuery(id+"F20.wireOp",EDGE,"E57.right"),sQuery(id+"F20.wireOp",EDGE,"E58.top"),sQuery(id+"F20.wireOp",EDGE,"E58.left"),sQuery(id+"F20.wireOp",EDGE,"E58.right"),sQuery(id+"F20.wireOp",EDGE,"E60.trimOffspring"),sQuery(id+"F20.wireOp",EDGE,"E61.trimOffspring"),sQuery(id+"F20.wireOp",EDGE,"E62.trimOffspring"),sQuery(id+"F20.wireOp",EDGE,"E63.filletArc"),sQuery(id+"F20.wireOp",EDGE,"E65"),sQuery(id+"F20.wireOp",EDGE,"E66.trimOffspring"),sQuery(id+"F20.wireOp",EDGE,"E67.filletArc"),sQuery(id+"F20.wireOp",EDGE,"E68.filletArc"),sQuery(id+"F20.wireOp",EDGE,"E69"),sQuery(id+"F20.wireOp",EDGE,"E70"),sQuery(id+"F20.wireOp",EDGE,"E71"),sQuery(id+"F20.wireOp",EDGE,"E72"),sQuery(id+"F20.wireOp",EDGE,"E73"),sQuery(id+"F20.wireOp",EDGE,"E74.MirrorCS"),sQuery(id+"F20.wireOp",EDGE,"E75.MirrorCS"),sQuery(id+"F20.wireOp",EDGE,"E76.MirrorC"),sQuery(id+"F20.wireOp",EDGE,"E77.MirrorCS"),sQuery(id+"F20.wireOp",EDGE,"E78.MirrorCS")])]}),"instanceName":"1"});
            var Q2;
            Q2=makeQuery(id+"F24.opExtrude","SWEPT_BODY",BODY,{"disambiguationData":[OSD([sQuery(id+"F23.wireOp",EDGE,"E79.bottom"),sQuery(id+"F23.wireOp",EDGE,"E79.top"),sQuery(id+"F23.wireOp",EDGE,"E79.left"),sQuery(id+"F23.wireOp",EDGE,"E79.right")])]});
            booleanBodies(context, id + "F25", {"operationType" : BooleanOperationType.SUBTRACTION, "tools" : qUnion([Q0, Q1]), "targets" : qUnion([Q2]), "keepTools" : true});
        }
        {
            var Q0;
            Q0=makeQuery(id+"F1.opExtrude","CAP_FACE",FACE,{"disambiguationData":[OSD([sQuery(id+"F0.wireOp",EDGE,"E4"),sQuery(id+"F0.wireOp",EDGE,"E5"),sQuery(id+"F0.wireOp",EDGE,"E6"),sQuery(id+"F0.wireOp",EDGE,"E7")])],"isStart":false});
            cPlane(context, id + "F26", {"entities" : qUnion([Q0]), "cplaneType" : CPlaneType.OFFSET, "offset" : 38 * mm, "oppositeDirection" : true, "width" : 150 * mm, "height" : 150 * mm});
        }
        {
            var Q0;
            Q0=qCreatedBy(id+"F26.planeOp",FACE);
            var sketch = newSketch(context, id + "F27", { "sketchPlane" : qUnion([Q0])});
            skLineSegment(sketch, "E80", {"start": v(-45, 70.93) * mm, "end": v(-45, 80.66) * mm});
            skLineSegment(sketch, "E81", {"start": v(-45, 80.66) * mm, "end": v(-45, 115.66) * mm});
            skLineSegment(sketch, "E82", {"start": v(-45, 115.66) * mm, "end": v(45, 115.66) * mm});
            skLineSegment(sketch, "E83", {"start": v(45, 115.66) * mm, "end": v(45, 80.66) * mm});
            skLineSegment(sketch, "E84", {"start": v(45, 80.66) * mm, "end": v(45, 70.93) * mm});
            skArc(sketch, "E85", {"start": v(-45, 70.93) * mm, "mid": v(0, -84) * mm, "end": v(45, 70.93) * mm});
            skLineSegment(sketch, "E86", {"start": v(0, 115.66) * mm, "end": v(0, -84) * mm, "construction": true});
            skLineSegment(sketch, "E87.bottom", {"start": v(-35, 55.66) * mm, "end": v(-25, 55.66) * mm});
            skLineSegment(sketch, "E87.top", {"start": v(-35, 35.66) * mm, "end": v(-25, 35.66) * mm});
            skLineSegment(sketch, "E87.left", {"start": v(-35, 55.66) * mm, "end": v(-35, 35.66) * mm});
            skLineSegment(sketch, "E87.right", {"start": v(-25, 55.66) * mm, "end": v(-25, 35.66) * mm});
            skLineSegment(sketch, "E88.MirrorCS", {"start": v(35, 55.66) * mm, "end": v(25, 55.66) * mm});
            skLineSegment(sketch, "E89.MirrorCS", {"start": v(25, 55.66) * mm, "end": v(25, 35.66) * mm});
            skLineSegment(sketch, "E90.MirrorCS", {"start": v(35, 35.66) * mm, "end": v(25, 35.66) * mm});
            skLineSegment(sketch, "E91.MirrorCS", {"start": v(35, 55.66) * mm, "end": v(35, 35.66) * mm});
            skCircle(sketch, "E92", {"center": v(-30, 99.66) * mm, "radius": 5.25 * mm});
            skCircle(sketch, "E93", {"center": v(0, 99.66) * mm, "radius": 5.25 * mm});
            skCircle(sketch, "E94", {"center": v(30, 99.66) * mm, "radius": 5.25 * mm});
            skSolve(sketch);
        }
        {
            var Q0;
            Q0 = qSketchRegion(id + "F27", true);
            extrude(context, id + "F28", {"entities" : qUnion([Q0]), "depth" : 10 * mm});
        }
        {
            var Q0;
            Q0=makeQuery(id+"F28.opExtrude","SWEPT_BODY",BODY,{"disambiguationData":[OSD([sQuery(id+"F27.wireOp",EDGE,"E80"),sQuery(id+"F27.wireOp",EDGE,"E81"),sQuery(id+"F27.wireOp",EDGE,"E82"),sQuery(id+"F27.wireOp",EDGE,"E83"),sQuery(id+"F27.wireOp",EDGE,"E84"),sQuery(id+"F27.wireOp",EDGE,"E85"),sQuery(id+"F27.wireOp",EDGE,"E87.bottom"),sQuery(id+"F27.wireOp",EDGE,"E87.top"),sQuery(id+"F27.wireOp",EDGE,"E87.left"),sQuery(id+"F27.wireOp",EDGE,"E87.right"),sQuery(id+"F27.wireOp",EDGE,"E88.MirrorCS"),sQuery(id+"F27.wireOp",EDGE,"E89.MirrorCS"),sQuery(id+"F27.wireOp",EDGE,"E90.MirrorCS"),sQuery(id+"F27.wireOp",EDGE,"E91.MirrorCS"),sQuery(id+"F27.wireOp",EDGE,"E92"),sQuery(id+"F27.wireOp",EDGE,"E93"),sQuery(id+"F27.wireOp",EDGE,"E94")])]});
            var Q1;
            Q1=qCreatedBy(id+"F14.planeOp",FACE);
            mirror(context, id + "F29", {"entities" : qUnion([Q0]), "mirrorPlane" : qUnion([Q1])});
        }
        {
            var Q0;
            Q0=qCreatedBy(makeId("Right.planeOp"),FACE);
            var sketch = newSketch(context, id + "F30", { "sketchPlane" : qUnion([Q0])});
            skLineSegment(sketch, "E95", {"start": v(-96, -69) * mm, "end": v(-86, -69) * mm});
            skLineSegment(sketch, "E96", {"start": v(-86, -69) * mm, "end": v(-86, -84) * mm});
            skLineSegment(sketch, "E97", {"start": v(-86, -84) * mm, "end": v(-50, -84) * mm});
            skLineSegment(sketch, "E98", {"start": v(-50, -84) * mm, "end": v(-50, -39) * mm, "construction": true});
            skLineSegment(sketch, "E99", {"start": v(-50, -39) * mm, "end": v(-62, -39) * mm});
            skLineSegment(sketch, "E100", {"start": v(-78, -39) * mm, "end": v(-96, -51) * mm});
            skLineSegment(sketch, "E101", {"start": v(-96, -51) * mm, "end": v(-96, -69) * mm});
            skLineSegment(sketch, "E102", {"start": v(-62, -84) * mm, "end": v(-72, -84) * mm, "construction": true});
            skLineSegment(sketch, "E103.MirrorCS", {"start": v(-50, -39) * mm, "end": v(-38, -39) * mm});
            skLineSegment(sketch, "E104.MirrorCS", {"start": v(-22, -39) * mm, "end": v(-4, -51) * mm});
            skLineSegment(sketch, "E105.MirrorCS", {"start": v(-4, -51) * mm, "end": v(-4, -69) * mm});
            skLineSegment(sketch, "E106.MirrorCS", {"start": v(-4, -69) * mm, "end": v(-14, -69) * mm});
            skLineSegment(sketch, "E107.MirrorCS", {"start": v(-14, -69) * mm, "end": v(-14, -84) * mm});
            skLineSegment(sketch, "E108.MirrorCS", {"start": v(-14, -84) * mm, "end": v(-50, -84) * mm});
            skLineSegment(sketch, "E109.top", {"start": v(-72, -59) * mm, "end": v(-62, -59) * mm});
            skLineSegment(sketch, "E109.left", {"start": v(-72, -39) * mm, "end": v(-72, -59) * mm});
            skLineSegment(sketch, "E109.right", {"start": v(-62, -39) * mm, "end": v(-62, -59) * mm});
            skLineSegment(sketch, "E110.top", {"start": v(-38, -59) * mm, "end": v(-28, -59) * mm});
            skLineSegment(sketch, "E110.left", {"start": v(-38, -39) * mm, "end": v(-38, -59) * mm});
            skLineSegment(sketch, "E110.right", {"start": v(-28, -39) * mm, "end": v(-28, -59) * mm});
            skLineSegment(sketch, "E111.trimOffspring", {"start": v(-72, -39) * mm, "end": v(-78, -39) * mm});
            skLineSegment(sketch, "E112.trimOffspring", {"start": v(-28, -39) * mm, "end": v(-22, -39) * mm});
            skSolve(sketch);
        }
        {
            var Q0;
            Q0 = qSketchRegion(id + "F30", true);
            extrude(context, id + "F31", {"entities" : qUnion([Q0]), "depth" : 5 * mm, "hasSecondDirection" : true, "secondDirectionOppositeDirection" : true, "secondDirectionDepth" : 5 * mm});
        }
        {
            var Q0;
            Q0=makeQuery(id+"F31.opExtrude","SWEPT_BODY",BODY,{"disambiguationData":[OSD([sQuery(id+"F30.wireOp",EDGE,"E95"),sQuery(id+"F30.wireOp",EDGE,"E96"),sQuery(id+"F30.wireOp",EDGE,"E97"),sQuery(id+"F30.wireOp",EDGE,"E99"),sQuery(id+"F30.wireOp",EDGE,"E100"),sQuery(id+"F30.wireOp",EDGE,"E101"),sQuery(id+"F30.wireOp",EDGE,"E103.MirrorCS"),sQuery(id+"F30.wireOp",EDGE,"E104.MirrorCS"),sQuery(id+"F30.wireOp",EDGE,"E105.MirrorCS"),sQuery(id+"F30.wireOp",EDGE,"E106.MirrorCS"),sQuery(id+"F30.wireOp",EDGE,"E107.MirrorCS"),sQuery(id+"F30.wireOp",EDGE,"E108.MirrorCS"),sQuery(id+"F30.wireOp",EDGE,"E109.top"),sQuery(id+"F30.wireOp",EDGE,"E109.left"),sQuery(id+"F30.wireOp",EDGE,"E109.right"),sQuery(id+"F30.wireOp",EDGE,"E110.top"),sQuery(id+"F30.wireOp",EDGE,"E110.left"),sQuery(id+"F30.wireOp",EDGE,"E110.right"),sQuery(id+"F30.wireOp",EDGE,"E111.trimOffspring"),sQuery(id+"F30.wireOp",EDGE,"E112.trimOffspring")])]});
            var Q1;
            Q1=makeQuery(id+"F28.opExtrude","SWEPT_BODY",BODY,{"disambiguationData":[OSD([sQuery(id+"F27.wireOp",EDGE,"E80"),sQuery(id+"F27.wireOp",EDGE,"E81"),sQuery(id+"F27.wireOp",EDGE,"E82"),sQuery(id+"F27.wireOp",EDGE,"E83"),sQuery(id+"F27.wireOp",EDGE,"E84"),sQuery(id+"F27.wireOp",EDGE,"E85"),sQuery(id+"F27.wireOp",EDGE,"E87.bottom"),sQuery(id+"F27.wireOp",EDGE,"E87.top"),sQuery(id+"F27.wireOp",EDGE,"E87.left"),sQuery(id+"F27.wireOp",EDGE,"E87.right"),sQuery(id+"F27.wireOp",EDGE,"E88.MirrorCS"),sQuery(id+"F27.wireOp",EDGE,"E89.MirrorCS"),sQuery(id+"F27.wireOp",EDGE,"E90.MirrorCS"),sQuery(id+"F27.wireOp",EDGE,"E91.MirrorCS"),sQuery(id+"F27.wireOp",EDGE,"E92"),sQuery(id+"F27.wireOp",EDGE,"E93"),sQuery(id+"F27.wireOp",EDGE,"E94")])]});
            var Q2;
            Q2=makeQuery(id+"F29.opPattern","COPY",BODY,{"derivedFrom":makeQuery(id+"F28.opExtrude","SWEPT_BODY",BODY,{"disambiguationData":[OSD([sQuery(id+"F27.wireOp",EDGE,"E80"),sQuery(id+"F27.wireOp",EDGE,"E81"),sQuery(id+"F27.wireOp",EDGE,"E82"),sQuery(id+"F27.wireOp",EDGE,"E83"),sQuery(id+"F27.wireOp",EDGE,"E84"),sQuery(id+"F27.wireOp",EDGE,"E85"),sQuery(id+"F27.wireOp",EDGE,"E87.bottom"),sQuery(id+"F27.wireOp",EDGE,"E87.top"),sQuery(id+"F27.wireOp",EDGE,"E87.left"),sQuery(id+"F27.wireOp",EDGE,"E87.right"),sQuery(id+"F27.wireOp",EDGE,"E88.MirrorCS"),sQuery(id+"F27.wireOp",EDGE,"E89.MirrorCS"),sQuery(id+"F27.wireOp",EDGE,"E90.MirrorCS"),sQuery(id+"F27.wireOp",EDGE,"E91.MirrorCS"),sQuery(id+"F27.wireOp",EDGE,"E92"),sQuery(id+"F27.wireOp",EDGE,"E93"),sQuery(id+"F27.wireOp",EDGE,"E94")])]}),"instanceName":"1"});
            booleanBodies(context, id + "F32", {"operationType" : BooleanOperationType.SUBTRACTION, "tools" : qUnion([Q0]), "targets" : qUnion([Q1, Q2]), "keepTools" : true});
        }
        {
            var Q0;
            Q0=makeQuery(id+"F31.opExtrude","SWEPT_BODY",BODY,{"disambiguationData":[OSD([sQuery(id+"F30.wireOp",EDGE,"E95"),sQuery(id+"F30.wireOp",EDGE,"E96"),sQuery(id+"F30.wireOp",EDGE,"E97"),sQuery(id+"F30.wireOp",EDGE,"E99"),sQuery(id+"F30.wireOp",EDGE,"E100"),sQuery(id+"F30.wireOp",EDGE,"E101"),sQuery(id+"F30.wireOp",EDGE,"E103.MirrorCS"),sQuery(id+"F30.wireOp",EDGE,"E104.MirrorCS"),sQuery(id+"F30.wireOp",EDGE,"E105.MirrorCS"),sQuery(id+"F30.wireOp",EDGE,"E106.MirrorCS"),sQuery(id+"F30.wireOp",EDGE,"E107.MirrorCS"),sQuery(id+"F30.wireOp",EDGE,"E108.MirrorCS"),sQuery(id+"F30.wireOp",EDGE,"E109.top"),sQuery(id+"F30.wireOp",EDGE,"E109.left"),sQuery(id+"F30.wireOp",EDGE,"E109.right"),sQuery(id+"F30.wireOp",EDGE,"E110.top"),sQuery(id+"F30.wireOp",EDGE,"E110.left"),sQuery(id+"F30.wireOp",EDGE,"E110.right"),sQuery(id+"F30.wireOp",EDGE,"E111.trimOffspring"),sQuery(id+"F30.wireOp",EDGE,"E112.trimOffspring")])]});
            var Q1;
            {var subQ11=sQuery(id+"F27.wireOp",EDGE,"E85");var subQ12=sQuery(id+"F27.wireOp",EDGE,"E84");var subQ13=sQuery(id+"F27.wireOp",EDGE,"E83");Q1=makeQuery(id+"F32.opBoolean","SPLIT",FACE,{"disambiguationData":[TD([makeQuery(id+"F28.opExtrude","SWEPT_FACE",FACE,{"disambiguationData":[OSD([subQ13,subQ12])]})])],"derivedFrom":makeQuery(id+"F28.opExtrude","SWEPT_FACE",FACE,{"disambiguationData":[OSD([subQ11])]})});}
            circularPattern(context, id + "F33", {"entities" : qUnion([Q0]), "axis" : qUnion([Q1]), "angle" : 56 * degree, "instanceCount" : 3});
        }
        {
            var Q0;
            Q0=makeQuery(id+"F31.opExtrude","SWEPT_BODY",BODY,{"disambiguationData":[OSD([sQuery(id+"F30.wireOp",EDGE,"E95"),sQuery(id+"F30.wireOp",EDGE,"E96"),sQuery(id+"F30.wireOp",EDGE,"E97"),sQuery(id+"F30.wireOp",EDGE,"E99"),sQuery(id+"F30.wireOp",EDGE,"E100"),sQuery(id+"F30.wireOp",EDGE,"E101"),sQuery(id+"F30.wireOp",EDGE,"E103.MirrorCS"),sQuery(id+"F30.wireOp",EDGE,"E104.MirrorCS"),sQuery(id+"F30.wireOp",EDGE,"E105.MirrorCS"),sQuery(id+"F30.wireOp",EDGE,"E106.MirrorCS"),sQuery(id+"F30.wireOp",EDGE,"E107.MirrorCS"),sQuery(id+"F30.wireOp",EDGE,"E108.MirrorCS"),sQuery(id+"F30.wireOp",EDGE,"E109.top"),sQuery(id+"F30.wireOp",EDGE,"E109.left"),sQuery(id+"F30.wireOp",EDGE,"E109.right"),sQuery(id+"F30.wireOp",EDGE,"E110.top"),sQuery(id+"F30.wireOp",EDGE,"E110.left"),sQuery(id+"F30.wireOp",EDGE,"E110.right"),sQuery(id+"F30.wireOp",EDGE,"E111.trimOffspring"),sQuery(id+"F30.wireOp",EDGE,"E112.trimOffspring")])]});
            var Q1;
            {var subQ0=sQuery(id+"F27.wireOp",EDGE,"E81");var subQ1=sQuery(id+"F27.wireOp",EDGE,"E80");var subQ13=sQuery(id+"F27.wireOp",EDGE,"E85");Q1=makeQuery(id+"F32.opBoolean","SPLIT",FACE,{"disambiguationData":[TD([makeQuery(id+"F28.opExtrude","SWEPT_FACE",FACE,{"disambiguationData":[OSD([subQ1,subQ0])]})])],"derivedFrom":makeQuery(id+"F28.opExtrude","SWEPT_FACE",FACE,{"disambiguationData":[OSD([subQ13])]})});}
            circularPattern(context, id + "F34", {"entities" : qUnion([Q0]), "axis" : qUnion([Q1]), "angle" : 56 * degree, "instanceCount" : 3, "oppositeDirection" : true});
        }
        {
            var Q0;
            Q0=makeQuery(id+"F31.opExtrude","SWEPT_FACE",FACE,{"disambiguationData":[OSD([sQuery(id+"F30.wireOp",EDGE,"E96")])]});
            var sketch = newSketch(context, id + "F35", { "sketchPlane" : qUnion([Q0])});
            skCircle(sketch, "E113", {"center": v(0, 0) * mm, "radius": 84 * mm});
            skCircle(sketch, "E114", {"center": v(0, 0) * mm, "radius": 54 * mm, "construction": true});
            skCircle(sketch, "E115", {"center": v(0, 0) * mm, "radius": 64 * mm, "construction": true});
            skArc(sketch, "E116", {"start": v(-44.9, 30) * mm, "mid": v(-50.07, 20.23) * mm, "end": v(-53.14, 9.6) * mm});
            skArc(sketch, "E117", {"start": v(-63.58, 7.35) * mm, "mid": v(-63.65, -6.69) * mm, "end": v(-60.66, -20.4) * mm});
            skLineSegment(sketch, "E118", {"start": v(-63.58, 7.35) * mm, "end": v(-53.14, 9.6) * mm});
            skLineSegment(sketch, "E119", {"start": v(-60.66, -20.4) * mm, "end": v(-49.98, -20.44) * mm});
            skLineSegment(sketch, "E120", {"start": v(0, 0) * mm, "end": v(-63.65, -6.69) * mm, "construction": true});
            skArc(sketch, "E121.1.0", {"start": v(-49.98, -20.44) * mm, "mid": v(-44.77, -30.2) * mm, "end": v(-37.68, -38.68) * mm});
            skLineSegment(sketch, "E121.1.1", {"start": v(-41.65, -48.6) * mm, "end": v(-37.68, -38.68) * mm});
            skArc(sketch, "E121.1.2", {"start": v(-41.65, -48.6) * mm, "mid": v(-30.05, -56.5) * mm, "end": v(-17, -61.7) * mm});
            skLineSegment(sketch, "E121.1.3", {"start": v(-17, -61.7) * mm, "end": v(-11, -52.87) * mm});
            skArc(sketch, "E121.2.0", {"start": v(-11, -52.87) * mm, "mid": v(0, -54) * mm, "end": v(11, -52.87) * mm});
            skLineSegment(sketch, "E121.2.1", {"start": v(17, -61.7) * mm, "end": v(11, -52.87) * mm});
            skArc(sketch, "E121.2.2", {"start": v(17, -61.7) * mm, "mid": v(30.05, -56.5) * mm, "end": v(41.65, -48.6) * mm});
            skLineSegment(sketch, "E121.2.3", {"start": v(41.65, -48.6) * mm, "end": v(37.68, -38.68) * mm});
            skArc(sketch, "E121.3.0", {"start": v(37.68, -38.68) * mm, "mid": v(44.77, -30.2) * mm, "end": v(49.98, -20.44) * mm});
            skLineSegment(sketch, "E121.3.1", {"start": v(60.66, -20.4) * mm, "end": v(49.98, -20.44) * mm});
            skArc(sketch, "E121.3.2", {"start": v(60.66, -20.4) * mm, "mid": v(63.65, -6.69) * mm, "end": v(63.58, 7.35) * mm});
            skLineSegment(sketch, "E121.3.3", {"start": v(63.58, 7.35) * mm, "end": v(53.14, 9.6) * mm});
            skArc(sketch, "E121.4.0", {"start": v(53.14, 9.6) * mm, "mid": v(50.07, 20.23) * mm, "end": v(44.9, 30) * mm});
            skLineSegment(sketch, "E121.4.1", {"start": v(50.84, 38.88) * mm, "end": v(44.9, 30) * mm});
            skLineSegment(sketch, "E121.anchor1", {"start": v(0, 0) * mm, "end": v(-53.14, 9.6) * mm, "construction": true});
            skLineSegment(sketch, "E121.anchor2", {"start": v(0, 0) * mm, "end": v(44.9, 30) * mm, "construction": true});
            skLineSegment(sketch, "E122", {"start": v(-44.9, 30) * mm, "end": v(-50.84, 38.88) * mm});
            skArc(sketch, "E123", {"start": v(50.84, 38.88) * mm, "mid": v(0, 64) * mm, "end": v(-50.84, 38.88) * mm});
            skSolve(sketch);
        }
        {
            var Q0;
            Q0 = qSketchRegion(id + "F35", true);
            extrude(context, id + "F36", {"entities" : qUnion([Q0]), "depth" : 10 * mm});
        }
        {
            var Q0;
            Q0=makeQuery(id+"F33.opPattern","COPY",BODY,{"derivedFrom":makeQuery(id+"F31.opExtrude","SWEPT_BODY",BODY,{"disambiguationData":[OSD([sQuery(id+"F30.wireOp",EDGE,"E95"),sQuery(id+"F30.wireOp",EDGE,"E96"),sQuery(id+"F30.wireOp",EDGE,"E97"),sQuery(id+"F30.wireOp",EDGE,"E99"),sQuery(id+"F30.wireOp",EDGE,"E100"),sQuery(id+"F30.wireOp",EDGE,"E101"),sQuery(id+"F30.wireOp",EDGE,"E103.MirrorCS"),sQuery(id+"F30.wireOp",EDGE,"E104.MirrorCS"),sQuery(id+"F30.wireOp",EDGE,"E105.MirrorCS"),sQuery(id+"F30.wireOp",EDGE,"E106.MirrorCS"),sQuery(id+"F30.wireOp",EDGE,"E107.MirrorCS"),sQuery(id+"F30.wireOp",EDGE,"E108.MirrorCS"),sQuery(id+"F30.wireOp",EDGE,"E109.top"),sQuery(id+"F30.wireOp",EDGE,"E109.left"),sQuery(id+"F30.wireOp",EDGE,"E109.right"),sQuery(id+"F30.wireOp",EDGE,"E110.top"),sQuery(id+"F30.wireOp",EDGE,"E110.left"),sQuery(id+"F30.wireOp",EDGE,"E110.right"),sQuery(id+"F30.wireOp",EDGE,"E111.trimOffspring"),sQuery(id+"F30.wireOp",EDGE,"E112.trimOffspring")])]}),"instanceName":"2"});
            var Q1;
            Q1=makeQuery(id+"F33.opPattern","COPY",BODY,{"derivedFrom":makeQuery(id+"F31.opExtrude","SWEPT_BODY",BODY,{"disambiguationData":[OSD([sQuery(id+"F30.wireOp",EDGE,"E95"),sQuery(id+"F30.wireOp",EDGE,"E96"),sQuery(id+"F30.wireOp",EDGE,"E97"),sQuery(id+"F30.wireOp",EDGE,"E99"),sQuery(id+"F30.wireOp",EDGE,"E100"),sQuery(id+"F30.wireOp",EDGE,"E101"),sQuery(id+"F30.wireOp",EDGE,"E103.MirrorCS"),sQuery(id+"F30.wireOp",EDGE,"E104.MirrorCS"),sQuery(id+"F30.wireOp",EDGE,"E105.MirrorCS"),sQuery(id+"F30.wireOp",EDGE,"E106.MirrorCS"),sQuery(id+"F30.wireOp",EDGE,"E107.MirrorCS"),sQuery(id+"F30.wireOp",EDGE,"E108.MirrorCS"),sQuery(id+"F30.wireOp",EDGE,"E109.top"),sQuery(id+"F30.wireOp",EDGE,"E109.left"),sQuery(id+"F30.wireOp",EDGE,"E109.right"),sQuery(id+"F30.wireOp",EDGE,"E110.top"),sQuery(id+"F30.wireOp",EDGE,"E110.left"),sQuery(id+"F30.wireOp",EDGE,"E110.right"),sQuery(id+"F30.wireOp",EDGE,"E111.trimOffspring"),sQuery(id+"F30.wireOp",EDGE,"E112.trimOffspring")])]}),"instanceName":"1"});
            var Q2;
            Q2=makeQuery(id+"F31.opExtrude","SWEPT_BODY",BODY,{"disambiguationData":[OSD([sQuery(id+"F30.wireOp",EDGE,"E95"),sQuery(id+"F30.wireOp",EDGE,"E96"),sQuery(id+"F30.wireOp",EDGE,"E97"),sQuery(id+"F30.wireOp",EDGE,"E99"),sQuery(id+"F30.wireOp",EDGE,"E100"),sQuery(id+"F30.wireOp",EDGE,"E101"),sQuery(id+"F30.wireOp",EDGE,"E103.MirrorCS"),sQuery(id+"F30.wireOp",EDGE,"E104.MirrorCS"),sQuery(id+"F30.wireOp",EDGE,"E105.MirrorCS"),sQuery(id+"F30.wireOp",EDGE,"E106.MirrorCS"),sQuery(id+"F30.wireOp",EDGE,"E107.MirrorCS"),sQuery(id+"F30.wireOp",EDGE,"E108.MirrorCS"),sQuery(id+"F30.wireOp",EDGE,"E109.top"),sQuery(id+"F30.wireOp",EDGE,"E109.left"),sQuery(id+"F30.wireOp",EDGE,"E109.right"),sQuery(id+"F30.wireOp",EDGE,"E110.top"),sQuery(id+"F30.wireOp",EDGE,"E110.left"),sQuery(id+"F30.wireOp",EDGE,"E110.right"),sQuery(id+"F30.wireOp",EDGE,"E111.trimOffspring"),sQuery(id+"F30.wireOp",EDGE,"E112.trimOffspring")])]});
            var Q3;
            Q3=makeQuery(id+"F34.opPattern","COPY",BODY,{"derivedFrom":makeQuery(id+"F31.opExtrude","SWEPT_BODY",BODY,{"disambiguationData":[OSD([sQuery(id+"F30.wireOp",EDGE,"E95"),sQuery(id+"F30.wireOp",EDGE,"E96"),sQuery(id+"F30.wireOp",EDGE,"E97"),sQuery(id+"F30.wireOp",EDGE,"E99"),sQuery(id+"F30.wireOp",EDGE,"E100"),sQuery(id+"F30.wireOp",EDGE,"E101"),sQuery(id+"F30.wireOp",EDGE,"E103.MirrorCS"),sQuery(id+"F30.wireOp",EDGE,"E104.MirrorCS"),sQuery(id+"F30.wireOp",EDGE,"E105.MirrorCS"),sQuery(id+"F30.wireOp",EDGE,"E106.MirrorCS"),sQuery(id+"F30.wireOp",EDGE,"E107.MirrorCS"),sQuery(id+"F30.wireOp",EDGE,"E108.MirrorCS"),sQuery(id+"F30.wireOp",EDGE,"E109.top"),sQuery(id+"F30.wireOp",EDGE,"E109.left"),sQuery(id+"F30.wireOp",EDGE,"E109.right"),sQuery(id+"F30.wireOp",EDGE,"E110.top"),sQuery(id+"F30.wireOp",EDGE,"E110.left"),sQuery(id+"F30.wireOp",EDGE,"E110.right"),sQuery(id+"F30.wireOp",EDGE,"E111.trimOffspring"),sQuery(id+"F30.wireOp",EDGE,"E112.trimOffspring")])]}),"instanceName":"1"});
            var Q4;
            Q4=makeQuery(id+"F34.opPattern","COPY",BODY,{"derivedFrom":makeQuery(id+"F31.opExtrude","SWEPT_BODY",BODY,{"disambiguationData":[OSD([sQuery(id+"F30.wireOp",EDGE,"E95"),sQuery(id+"F30.wireOp",EDGE,"E96"),sQuery(id+"F30.wireOp",EDGE,"E97"),sQuery(id+"F30.wireOp",EDGE,"E99"),sQuery(id+"F30.wireOp",EDGE,"E100"),sQuery(id+"F30.wireOp",EDGE,"E101"),sQuery(id+"F30.wireOp",EDGE,"E103.MirrorCS"),sQuery(id+"F30.wireOp",EDGE,"E104.MirrorCS"),sQuery(id+"F30.wireOp",EDGE,"E105.MirrorCS"),sQuery(id+"F30.wireOp",EDGE,"E106.MirrorCS"),sQuery(id+"F30.wireOp",EDGE,"E107.MirrorCS"),sQuery(id+"F30.wireOp",EDGE,"E108.MirrorCS"),sQuery(id+"F30.wireOp",EDGE,"E109.top"),sQuery(id+"F30.wireOp",EDGE,"E109.left"),sQuery(id+"F30.wireOp",EDGE,"E109.right"),sQuery(id+"F30.wireOp",EDGE,"E110.top"),sQuery(id+"F30.wireOp",EDGE,"E110.left"),sQuery(id+"F30.wireOp",EDGE,"E110.right"),sQuery(id+"F30.wireOp",EDGE,"E111.trimOffspring"),sQuery(id+"F30.wireOp",EDGE,"E112.trimOffspring")])]}),"instanceName":"2"});
            var Q5;
            Q5=makeQuery(id+"F36.opExtrude","SWEPT_BODY",BODY,{"disambiguationData":[OSD([sQuery(id+"F35.wireOp",EDGE,"E113"),sQuery(id+"F35.wireOp",EDGE,"E116"),sQuery(id+"F35.wireOp",EDGE,"E117"),sQuery(id+"F35.wireOp",EDGE,"E118"),sQuery(id+"F35.wireOp",EDGE,"E119"),sQuery(id+"F35.wireOp",EDGE,"E121.1.0"),sQuery(id+"F35.wireOp",EDGE,"E121.1.1"),sQuery(id+"F35.wireOp",EDGE,"E121.1.2"),sQuery(id+"F35.wireOp",EDGE,"E121.1.3"),sQuery(id+"F35.wireOp",EDGE,"E121.2.0"),sQuery(id+"F35.wireOp",EDGE,"E121.2.1"),sQuery(id+"F35.wireOp",EDGE,"E121.2.2"),sQuery(id+"F35.wireOp",EDGE,"E121.2.3"),sQuery(id+"F35.wireOp",EDGE,"E121.3.0"),sQuery(id+"F35.wireOp",EDGE,"E121.3.1"),sQuery(id+"F35.wireOp",EDGE,"E121.3.2"),sQuery(id+"F35.wireOp",EDGE,"E121.3.3"),sQuery(id+"F35.wireOp",EDGE,"E121.4.0"),sQuery(id+"F35.wireOp",EDGE,"E121.4.1"),sQuery(id+"F35.wireOp",EDGE,"E122"),sQuery(id+"F35.wireOp",EDGE,"E123")])]});
            booleanBodies(context, id + "F37", {"operationType" : BooleanOperationType.SUBTRACTION, "tools" : qUnion([Q0, Q1, Q2, Q3, Q4]), "targets" : qUnion([Q5]), "keepTools" : true});
        }
        {
            var Q0;
            Q0=makeQuery(id+"F36.opExtrude","CAP_FACE",FACE,{"disambiguationData":[OSD([sQuery(id+"F35.wireOp",EDGE,"E113"),sQuery(id+"F35.wireOp",EDGE,"E116"),sQuery(id+"F35.wireOp",EDGE,"E117"),sQuery(id+"F35.wireOp",EDGE,"E118"),sQuery(id+"F35.wireOp",EDGE,"E119"),sQuery(id+"F35.wireOp",EDGE,"E121.1.0"),sQuery(id+"F35.wireOp",EDGE,"E121.1.1"),sQuery(id+"F35.wireOp",EDGE,"E121.1.2"),sQuery(id+"F35.wireOp",EDGE,"E121.1.3"),sQuery(id+"F35.wireOp",EDGE,"E121.2.0"),sQuery(id+"F35.wireOp",EDGE,"E121.2.1"),sQuery(id+"F35.wireOp",EDGE,"E121.2.2"),sQuery(id+"F35.wireOp",EDGE,"E121.2.3"),sQuery(id+"F35.wireOp",EDGE,"E121.3.0"),sQuery(id+"F35.wireOp",EDGE,"E121.3.1"),sQuery(id+"F35.wireOp",EDGE,"E121.3.2"),sQuery(id+"F35.wireOp",EDGE,"E121.3.3"),sQuery(id+"F35.wireOp",EDGE,"E121.4.0"),sQuery(id+"F35.wireOp",EDGE,"E121.4.1"),sQuery(id+"F35.wireOp",EDGE,"E122"),sQuery(id+"F35.wireOp",EDGE,"E123")])],"isStart":false});
            var sketch = newSketch(context, id + "F38", { "sketchPlane" : qUnion([Q0])});
            skArc(sketch, "E124", {"start": v(-45, 70.93) * mm, "mid": v(0, -84) * mm, "end": v(45, 70.93) * mm});
            skArc(sketch, "E125", {"start": v(-48.21, 76) * mm, "mid": v(0, -90) * mm, "end": v(48.21, 76) * mm});
            skLineSegment(sketch, "E126", {"start": v(-48.21, 76) * mm, "end": v(-45, 70.93) * mm});
            skLineSegment(sketch, "E127", {"start": v(48.21, 76) * mm, "end": v(45, 70.93) * mm});
            skSolve(sketch);
        }
        {
            var Q0;
            Q0 = qSketchRegion(id + "F38", true);
            extrude(context, id + "F39", {"entities" : qUnion([Q0]), "oppositeDirection" : true, "depth" : 96 * mm, "hasSecondDirection" : true, "secondDirectionOppositeDirection" : false, "secondDirectionDepth" : 4 * mm});
        }
        {
            var Q0;
            Q0=makeQuery(id+"F39.opExtrude","SWEPT_BODY",BODY,{"disambiguationData":[OSD([sQuery(id+"F38.wireOp",EDGE,"E124"),sQuery(id+"F38.wireOp",EDGE,"E125"),sQuery(id+"F38.wireOp",EDGE,"E126"),sQuery(id+"F38.wireOp",EDGE,"E127")])]});
            var Q1;
            Q1=makeQuery(id+"F33.opPattern","COPY",BODY,{"derivedFrom":makeQuery(id+"F31.opExtrude","SWEPT_BODY",BODY,{"disambiguationData":[OSD([sQuery(id+"F30.wireOp",EDGE,"E95"),sQuery(id+"F30.wireOp",EDGE,"E96"),sQuery(id+"F30.wireOp",EDGE,"E97"),sQuery(id+"F30.wireOp",EDGE,"E99"),sQuery(id+"F30.wireOp",EDGE,"E100"),sQuery(id+"F30.wireOp",EDGE,"E101"),sQuery(id+"F30.wireOp",EDGE,"E103.MirrorCS"),sQuery(id+"F30.wireOp",EDGE,"E104.MirrorCS"),sQuery(id+"F30.wireOp",EDGE,"E105.MirrorCS"),sQuery(id+"F30.wireOp",EDGE,"E106.MirrorCS"),sQuery(id+"F30.wireOp",EDGE,"E107.MirrorCS"),sQuery(id+"F30.wireOp",EDGE,"E108.MirrorCS"),sQuery(id+"F30.wireOp",EDGE,"E109.top"),sQuery(id+"F30.wireOp",EDGE,"E109.left"),sQuery(id+"F30.wireOp",EDGE,"E109.right"),sQuery(id+"F30.wireOp",EDGE,"E110.top"),sQuery(id+"F30.wireOp",EDGE,"E110.left"),sQuery(id+"F30.wireOp",EDGE,"E110.right"),sQuery(id+"F30.wireOp",EDGE,"E111.trimOffspring"),sQuery(id+"F30.wireOp",EDGE,"E112.trimOffspring")])]}),"instanceName":"2"});
            var Q2;
            Q2=makeQuery(id+"F33.opPattern","COPY",BODY,{"derivedFrom":makeQuery(id+"F31.opExtrude","SWEPT_BODY",BODY,{"disambiguationData":[OSD([sQuery(id+"F30.wireOp",EDGE,"E95"),sQuery(id+"F30.wireOp",EDGE,"E96"),sQuery(id+"F30.wireOp",EDGE,"E97"),sQuery(id+"F30.wireOp",EDGE,"E99"),sQuery(id+"F30.wireOp",EDGE,"E100"),sQuery(id+"F30.wireOp",EDGE,"E101"),sQuery(id+"F30.wireOp",EDGE,"E103.MirrorCS"),sQuery(id+"F30.wireOp",EDGE,"E104.MirrorCS"),sQuery(id+"F30.wireOp",EDGE,"E105.MirrorCS"),sQuery(id+"F30.wireOp",EDGE,"E106.MirrorCS"),sQuery(id+"F30.wireOp",EDGE,"E107.MirrorCS"),sQuery(id+"F30.wireOp",EDGE,"E108.MirrorCS"),sQuery(id+"F30.wireOp",EDGE,"E109.top"),sQuery(id+"F30.wireOp",EDGE,"E109.left"),sQuery(id+"F30.wireOp",EDGE,"E109.right"),sQuery(id+"F30.wireOp",EDGE,"E110.top"),sQuery(id+"F30.wireOp",EDGE,"E110.left"),sQuery(id+"F30.wireOp",EDGE,"E110.right"),sQuery(id+"F30.wireOp",EDGE,"E111.trimOffspring"),sQuery(id+"F30.wireOp",EDGE,"E112.trimOffspring")])]}),"instanceName":"1"});
            var Q3;
            Q3=makeQuery(id+"F31.opExtrude","SWEPT_BODY",BODY,{"disambiguationData":[OSD([sQuery(id+"F30.wireOp",EDGE,"E95"),sQuery(id+"F30.wireOp",EDGE,"E96"),sQuery(id+"F30.wireOp",EDGE,"E97"),sQuery(id+"F30.wireOp",EDGE,"E99"),sQuery(id+"F30.wireOp",EDGE,"E100"),sQuery(id+"F30.wireOp",EDGE,"E101"),sQuery(id+"F30.wireOp",EDGE,"E103.MirrorCS"),sQuery(id+"F30.wireOp",EDGE,"E104.MirrorCS"),sQuery(id+"F30.wireOp",EDGE,"E105.MirrorCS"),sQuery(id+"F30.wireOp",EDGE,"E106.MirrorCS"),sQuery(id+"F30.wireOp",EDGE,"E107.MirrorCS"),sQuery(id+"F30.wireOp",EDGE,"E108.MirrorCS"),sQuery(id+"F30.wireOp",EDGE,"E109.top"),sQuery(id+"F30.wireOp",EDGE,"E109.left"),sQuery(id+"F30.wireOp",EDGE,"E109.right"),sQuery(id+"F30.wireOp",EDGE,"E110.top"),sQuery(id+"F30.wireOp",EDGE,"E110.left"),sQuery(id+"F30.wireOp",EDGE,"E110.right"),sQuery(id+"F30.wireOp",EDGE,"E111.trimOffspring"),sQuery(id+"F30.wireOp",EDGE,"E112.trimOffspring")])]});
            var Q4;
            Q4=makeQuery(id+"F34.opPattern","COPY",BODY,{"derivedFrom":makeQuery(id+"F31.opExtrude","SWEPT_BODY",BODY,{"disambiguationData":[OSD([sQuery(id+"F30.wireOp",EDGE,"E95"),sQuery(id+"F30.wireOp",EDGE,"E96"),sQuery(id+"F30.wireOp",EDGE,"E97"),sQuery(id+"F30.wireOp",EDGE,"E99"),sQuery(id+"F30.wireOp",EDGE,"E100"),sQuery(id+"F30.wireOp",EDGE,"E101"),sQuery(id+"F30.wireOp",EDGE,"E103.MirrorCS"),sQuery(id+"F30.wireOp",EDGE,"E104.MirrorCS"),sQuery(id+"F30.wireOp",EDGE,"E105.MirrorCS"),sQuery(id+"F30.wireOp",EDGE,"E106.MirrorCS"),sQuery(id+"F30.wireOp",EDGE,"E107.MirrorCS"),sQuery(id+"F30.wireOp",EDGE,"E108.MirrorCS"),sQuery(id+"F30.wireOp",EDGE,"E109.top"),sQuery(id+"F30.wireOp",EDGE,"E109.left"),sQuery(id+"F30.wireOp",EDGE,"E109.right"),sQuery(id+"F30.wireOp",EDGE,"E110.top"),sQuery(id+"F30.wireOp",EDGE,"E110.left"),sQuery(id+"F30.wireOp",EDGE,"E110.right"),sQuery(id+"F30.wireOp",EDGE,"E111.trimOffspring"),sQuery(id+"F30.wireOp",EDGE,"E112.trimOffspring")])]}),"instanceName":"1"});
            var Q5;
            Q5=makeQuery(id+"F34.opPattern","COPY",BODY,{"derivedFrom":makeQuery(id+"F31.opExtrude","SWEPT_BODY",BODY,{"disambiguationData":[OSD([sQuery(id+"F30.wireOp",EDGE,"E95"),sQuery(id+"F30.wireOp",EDGE,"E96"),sQuery(id+"F30.wireOp",EDGE,"E97"),sQuery(id+"F30.wireOp",EDGE,"E99"),sQuery(id+"F30.wireOp",EDGE,"E100"),sQuery(id+"F30.wireOp",EDGE,"E101"),sQuery(id+"F30.wireOp",EDGE,"E103.MirrorCS"),sQuery(id+"F30.wireOp",EDGE,"E104.MirrorCS"),sQuery(id+"F30.wireOp",EDGE,"E105.MirrorCS"),sQuery(id+"F30.wireOp",EDGE,"E106.MirrorCS"),sQuery(id+"F30.wireOp",EDGE,"E107.MirrorCS"),sQuery(id+"F30.wireOp",EDGE,"E108.MirrorCS"),sQuery(id+"F30.wireOp",EDGE,"E109.top"),sQuery(id+"F30.wireOp",EDGE,"E109.left"),sQuery(id+"F30.wireOp",EDGE,"E109.right"),sQuery(id+"F30.wireOp",EDGE,"E110.top"),sQuery(id+"F30.wireOp",EDGE,"E110.left"),sQuery(id+"F30.wireOp",EDGE,"E110.right"),sQuery(id+"F30.wireOp",EDGE,"E111.trimOffspring"),sQuery(id+"F30.wireOp",EDGE,"E112.trimOffspring")])]}),"instanceName":"2"});
            booleanBodies(context, id + "F40", {"operationType" : BooleanOperationType.SUBTRACTION, "tools" : qUnion([Q0]), "targets" : qUnion([Q1, Q2, Q3, Q4, Q5]), "keepTools" : true});
        }
        {
            var Q0;
            Q0=makeQuery(id+"F28.opExtrude","SWEPT_FACE",FACE,{"disambiguationData":[OSD([sQuery(id+"F27.wireOp",EDGE,"E89.MirrorCS")])]});
            var sketch = newSketch(context, id + "F41", { "sketchPlane" : qUnion([Q0])});
            skLineSegment(sketch, "E128.bottom", {"start": v(-72, 65.66) * mm, "end": v(-28, 65.66) * mm});
            skLineSegment(sketch, "E128.top", {"start": v(-72, 25.66) * mm, "end": v(-28, 25.66) * mm});
            skLineSegment(sketch, "E128.left", {"start": v(-72, 65.66) * mm, "end": v(-72, 25.66) * mm});
            skLineSegment(sketch, "E128.right", {"start": v(-28, 65.66) * mm, "end": v(-28, 25.66) * mm});
            skSolve(sketch);
        }
        {
            var Q0;
            Q0 = qSketchRegion(id + "F41", true);
            extrude(context, id + "F42", {"entities" : qUnion([Q0]), "depth" : 10 * mm});
        }
        {
            var Q0;
            Q0=makeQuery(id+"F28.opExtrude","SWEPT_BODY",BODY,{"disambiguationData":[OSD([sQuery(id+"F27.wireOp",EDGE,"E80"),sQuery(id+"F27.wireOp",EDGE,"E81"),sQuery(id+"F27.wireOp",EDGE,"E82"),sQuery(id+"F27.wireOp",EDGE,"E83"),sQuery(id+"F27.wireOp",EDGE,"E84"),sQuery(id+"F27.wireOp",EDGE,"E85"),sQuery(id+"F27.wireOp",EDGE,"E87.bottom"),sQuery(id+"F27.wireOp",EDGE,"E87.top"),sQuery(id+"F27.wireOp",EDGE,"E87.left"),sQuery(id+"F27.wireOp",EDGE,"E87.right"),sQuery(id+"F27.wireOp",EDGE,"E88.MirrorCS"),sQuery(id+"F27.wireOp",EDGE,"E89.MirrorCS"),sQuery(id+"F27.wireOp",EDGE,"E90.MirrorCS"),sQuery(id+"F27.wireOp",EDGE,"E91.MirrorCS"),sQuery(id+"F27.wireOp",EDGE,"E92"),sQuery(id+"F27.wireOp",EDGE,"E93"),sQuery(id+"F27.wireOp",EDGE,"E94")])]});
            var Q1;
            Q1=makeQuery(id+"F29.opPattern","COPY",BODY,{"derivedFrom":makeQuery(id+"F28.opExtrude","SWEPT_BODY",BODY,{"disambiguationData":[OSD([sQuery(id+"F27.wireOp",EDGE,"E80"),sQuery(id+"F27.wireOp",EDGE,"E81"),sQuery(id+"F27.wireOp",EDGE,"E82"),sQuery(id+"F27.wireOp",EDGE,"E83"),sQuery(id+"F27.wireOp",EDGE,"E84"),sQuery(id+"F27.wireOp",EDGE,"E85"),sQuery(id+"F27.wireOp",EDGE,"E87.bottom"),sQuery(id+"F27.wireOp",EDGE,"E87.top"),sQuery(id+"F27.wireOp",EDGE,"E87.left"),sQuery(id+"F27.wireOp",EDGE,"E87.right"),sQuery(id+"F27.wireOp",EDGE,"E88.MirrorCS"),sQuery(id+"F27.wireOp",EDGE,"E89.MirrorCS"),sQuery(id+"F27.wireOp",EDGE,"E90.MirrorCS"),sQuery(id+"F27.wireOp",EDGE,"E91.MirrorCS"),sQuery(id+"F27.wireOp",EDGE,"E92"),sQuery(id+"F27.wireOp",EDGE,"E93"),sQuery(id+"F27.wireOp",EDGE,"E94")])]}),"instanceName":"1"});
            var Q2;
            Q2=makeQuery(id+"F42.opExtrude","SWEPT_BODY",BODY,{"disambiguationData":[OSD([sQuery(id+"F41.wireOp",EDGE,"E128.bottom"),sQuery(id+"F41.wireOp",EDGE,"E128.top"),sQuery(id+"F41.wireOp",EDGE,"E128.left"),sQuery(id+"F41.wireOp",EDGE,"E128.right")])]});
            booleanBodies(context, id + "F43", {"operationType" : BooleanOperationType.SUBTRACTION, "tools" : qUnion([Q0, Q1]), "targets" : qUnion([Q2]), "keepTools" : true});
        }
        {
            var Q0;
            Q0=makeQuery(id+"F13.opExtrude","CAP_FACE",FACE,{"disambiguationData":[OSD([sQuery(id+"F12.wireOp",EDGE,"E35"),sQuery(id+"F12.wireOp",EDGE,"E36"),sQuery(id+"F12.wireOp",EDGE,"E37"),sQuery(id+"F12.wireOp",EDGE,"E38"),sQuery(id+"F12.wireOp",EDGE,"E39"),sQuery(id+"F12.wireOp",EDGE,"E40"),sQuery(id+"F12.wireOp",EDGE,"E41"),sQuery(id+"F12.wireOp",EDGE,"E42"),sQuery(id+"F12.wireOp",EDGE,"E43"),sQuery(id+"F12.wireOp",EDGE,"E48.0.startCap"),sQuery(id+"F12.wireOp",EDGE,"E48.0.endCap"),sQuery(id+"F12.wireOp",EDGE,"E48.0.left"),sQuery(id+"F12.wireOp",EDGE,"E48.0.right"),sQuery(id+"F12.wireOp",EDGE,"E49"),sQuery(id+"F12.wireOp",EDGE,"E50.trimOffspring")])],"isStart":false});
            var sketch = newSketch(context, id + "F44", { "sketchPlane" : qUnion([Q0])});
            skLineSegment(sketch, "E129", {"start": v(35.38, -106.27) * mm, "end": v(0, 0) * mm});
            skArc(sketch, "E130.0.startCap", {"start": v(55.3, -99.63) * mm, "mid": v(42, -126.2) * mm, "end": v(15.45, -112.9) * mm});
            skArc(sketch, "E130.0.endCap", {"start": v(-19.92, -6.63) * mm, "mid": v(-6.63, 19.92) * mm, "end": v(19.92, 6.63) * mm});
            skLineSegment(sketch, "E130.0.left", {"start": v(15.45, -112.9) * mm, "end": v(-19.92, -6.63) * mm});
            skLineSegment(sketch, "E130.0.right", {"start": v(55.3, -99.63) * mm, "end": v(19.92, 6.63) * mm});
            skSolve(sketch);
        }
        {
            var Q0;
            Q0 = qSketchRegion(id + "F44", true);
            extrude(context, id + "F45", {"entities" : qUnion([Q0]), "depth" : 1 * mm});
        }
    });
